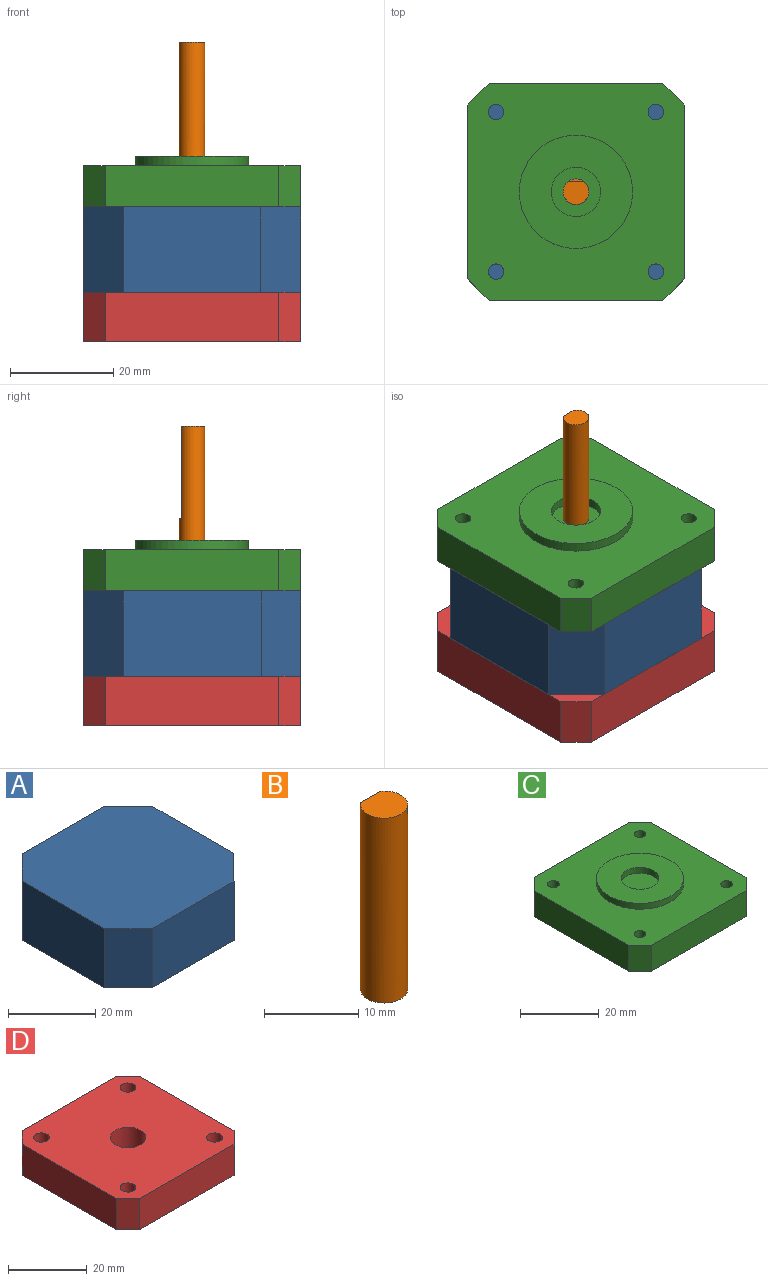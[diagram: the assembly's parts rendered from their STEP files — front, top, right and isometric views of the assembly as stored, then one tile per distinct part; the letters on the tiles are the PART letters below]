
ASSEMBLY  parts=4 mates=3
PART A: 10 faces, bbox 42.2x42.2x16.6 mm
  f0: plane 16.6x8mm, normal (0.71,-0.7,0), area 186.1mm2, adj f1,f7,f8,f9
  f1: plane 26.5x16.6mm, normal (1,0,0), area 439.9mm2, adj f0,f2,f8,f9
  f2: plane 16.6x7.7mm, normal (0.71,0.71,0), area 180.7mm2, adj f1,f3,f8,f9
  f3: plane 26.81x16.6mm, normal (0,1,0), area 445mm2, adj f2,f4,f8,f9
  f4: plane 16.6x7.7mm, normal (-0.71,0.71,0), area 180.7mm2, adj f3,f5,f8,f9
  f5: plane 26.81x16.6mm, normal (-1,0,0), area 445mm2, adj f4,f6,f8,f9
  f6: plane 16.6x7.85mm, normal (-0.7,-0.71,0), area 182.5mm2, adj f5,f7,f8,f9
  f7: plane 26.5x16.6mm, normal (0,-1,0), area 439.9mm2, adj f0,f6,f8,f9
  f8: plane 42.2x42.2mm, normal (0,0,1), area 1660mm2, adj f0,f1,f2,f3,f4,f5,f6,f7
  f9: plane 42.2x42.2mm, normal (0,0,-1), area 1660mm2, adj f0,f1,f2,f3,f4,f5,f6,f7
PART B: 5 faces, bbox 5x5x24 mm
  f0: cylinder r=2.5mm len=24mm, axis (0,0,-1), area 319.1mm2, adj f1,f2,f3,f4
  f1: plane 5x4.5mm, normal (0,0,1), area 18.6mm2, adj f0,f4
  f2: plane 5x5mm, normal (0,0,-1), area 19.6mm2, adj f0
  f3: plane 3x0.5mm, normal (0,0,1), area 1mm2, adj f0,f4
  f4: plane 18x3mm, normal (0,1,0), area 54mm2, adj f0,f1,f3
PART C: 18 faces, bbox 42.2x42.2x9.8 mm
  f0: plane 8x4.24mm, normal (0.71,-0.71,0), area 48mm2, adj f1,f10,f12,f13
  f1: plane 33.71x8mm, normal (1,0,0), area 269.7mm2, adj f0,f2,f12,f13
  f2: plane 8x4.24mm, normal (0.71,0.71,0), area 48mm2, adj f1,f3,f12,f13
  f3: plane 33.71x8mm, normal (0,1,0), area 269.7mm2, adj f2,f4,f12,f13
  f4: plane 8x4.24mm, normal (-0.71,0.71,0), area 48mm2, adj f3,f5,f12,f13
  f5: plane 33.71x8mm, normal (-1,0,0), area 269.7mm2, adj f4,f6,f12,f13
  f6: plane 8x4.24mm, normal (-0.71,-0.71,0), area 48mm2, adj f5,f10,f12,f13
  f7: cylinder r=1.5mm len=8mm, axis (0,0,-1), area 75.4mm2, adj f12,f13
  f8: cylinder r=1.5mm len=8mm, axis (0,0,-1), area 75.4mm2, adj f12,f13
  f9: cylinder r=1.5mm len=8mm, axis (0,0,-1), area 75.4mm2, adj f12,f13
  f10: plane 33.71x8mm, normal (0,-1,0), area 269.7mm2, adj f0,f6,f12,f13
  f11: cylinder r=1.5mm len=8mm, axis (0,0,-1), area 75.4mm2, adj f12,f13
  f12: plane 42.2x42.2mm, normal (0,0,1), area 1336.4mm2, adj f0,f1,f2,f3,f4,f5,f6,f7
  f13: plane 42.2x42.2mm, normal (0,0,-1), area 1716.6mm2, adj f0,f1,f2,f3,f4,f5,f6,f7
  f14: cylinder r=4.8mm len=9.6mm, axis (0,0,-1), area 54.3mm2, adj f16,f17
  f15: cylinder r=11mm len=22mm, axis (0,0,-1), area 124.4mm2, adj f12,f16
  f16: plane 22x22mm, normal (0,0,1), area 307.8mm2, adj f14,f15
  f17: plane 9.6x9.6mm, normal (0,0,1), area 72.4mm2, adj f14
PART D: 15 faces, bbox 42.2x42.2x9.6 mm
  f0: plane 9.6x4.24mm, normal (0.71,0.71,0), area 57.6mm2, adj f1,f12,f13,f14
  f1: plane 33.71x9.6mm, normal (0,1,0), area 323.7mm2, adj f0,f2,f13,f14
  f2: plane 9.6x4.24mm, normal (-0.71,0.71,0), area 57.6mm2, adj f1,f3,f13,f14
  f3: plane 33.71x9.6mm, normal (-1,0,0), area 323.7mm2, adj f2,f4,f13,f14
  f4: plane 9.6x4.24mm, normal (-0.71,-0.71,0), area 57.6mm2, adj f3,f5,f13,f14
  f5: plane 33.71x9.6mm, normal (0,-1,0), area 323.7mm2, adj f4,f6,f13,f14
  f6: plane 9.6x4.24mm, normal (0.71,-0.71,0), area 57.6mm2, adj f5,f12,f13,f14
  f7: cylinder r=2mm len=9.6mm, axis (0,0,-1), area 120.6mm2, adj f13,f14
  f8: cylinder r=2mm len=9.6mm, axis (0,0,-1), area 120.6mm2, adj f13,f14
  f9: cylinder r=2mm len=9.6mm, axis (0,0,-1), area 120.6mm2, adj f13,f14
  f10: cylinder r=2mm len=9.6mm, axis (0,0,-1), area 120.6mm2, adj f13,f14
  f11: cylinder r=4.5mm len=9.6mm, axis (0,0,-1), area 271.4mm2, adj f13,f14
  f12: plane 33.71x9.6mm, normal (1,0,0), area 323.7mm2, adj f0,f6,f13,f14
  f13: plane 42.2x42.2mm, normal (0,0,1), area 1631mm2, adj f0,f1,f2,f3,f4,f5,f6,f7
  f14: plane 42.2x42.2mm, normal (0,0,-1), area 1631mm2, adj f0,f1,f2,f3,f4,f5,f6,f7
PLACE A t=(-17.94,-0.19,-6.04)mm
PLACE B t=(-17.96,-0.17,-6.04)mm
PLACE C t=(-17.96,-0.17,-6.04)mm
PLACE D t=(-17.96,-0.17,-6.04)mm
MATE fastened B.f0 <-> C.f14  axis (0,0,-1) through (-17.96,-0.17,28.16)mm
MATE fastened C.f14 <-> A.f8  axis (0,0,-1) through (-17.96,-0.17,20.16)mm
MATE fastened A.f9 <-> D.f11  axis (0,0,-1) through (-17.96,-0.17,3.56)mm
